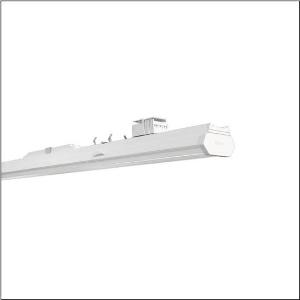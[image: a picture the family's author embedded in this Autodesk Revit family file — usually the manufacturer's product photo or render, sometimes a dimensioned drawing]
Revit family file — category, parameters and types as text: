
# Revit family: licross_r__21_protected_mo_52tp12dn4a5gd_0331
name_source: partatom
category: Lighting Fixtures
units: mm (PartAtom-declared; Revit-internal decimal feet)

## family parameters
Cut with Voids When Loaded = No
Host = Face
Light Source = No
Part Type = Normal
Room Calculation Point = No
Round Connector Dimension = Use Diameter
Shared = No

## types (1)
- --- (1 x LED, 1610 lm, 10.2 W, 4000K)
    Apparent Load = 10 VA
    CIE Flux Codes = 73 92 98 99 100
    Color Rendering = 80
    Color Temperature = 4000K
    Default Elevation = 1800 mm
    Description = Licross® 21 Protected MO, luminaire insert, of sheet steel, galvanised, coil coated, white, length: 1.500mm, width: 90mm, height: 103mm, LED rated luminous flux: 10.700lm, light colour: 840, SDCM (Standard Deviation of Colour Matching)MacAdam ≤ 3 SDCM (initial), control gear: DALI 2 (for two DALI lines), with plug, 6-pole, with phase selection, mains connection: 220..240V, AC/DC, 0/50..60Hz, rated input power: 62W, without changeover relay, for emergency light function, for central battery installations according to EN 60598-2-22, internal wiring halogen-free, primary light control with lens, of plastic, primary optical cover: cover, of PMMA, light emission: direct distribution, primary light characteristic: symmetric, protection rating (complete): IP64, insulation class (complete): insulation class I (protective earthing), certification: CE, ENEC, VDE, UKCA, protection symbol: D if used in an environment with conductive dust loads with corresponding accessories, impact resistance: IK06, permissible ambient temperature for indoor applications: -25..+35°C, standard: EN 60598-2-22, corresponds to IFS (International Featured Standards) requirements for safety and quality in the food industry, reducing of maximum allowable ambient temperature of 5°C with ceiling mounting, LABS conformity tested according to VDMA 24364:2018-05, packaging unit: 1 piece
    Height = 92 mm
    Lamp = 1 x LED
    Lamp Light Flux = 1610 lm
    Lamp Power = 10.2 W
    Lamp count = 1
    Length = 1500 mm
    Luminous efficacy = 158 lm/W
    Manufacturer = Siteco
    ModVariant = No
    Model = 52TP12DN4A5GD
    Mounting Place = Ceiling
    Mounting Type = Pendant
    Number of Poles = 1
    OnlyDefault = Yes
    Power Factor = 1
    Product Name = Licross® 21 Protected MO
    Product group = luminaire insert | ceiling pendant
    ProductGroupID = 901
    Protection Class = Protection class I
    Protection Degree = IP 64
    RLX_Detail_Level = 1
    RLX_Emergency_Light_Flux = 0 lm
    RLX_Emergency_Type = 0
    RLX_Emergency_Type_DB = No
    RlxData = <blob elided: 25073 chars, md5=40d94d71>
    Socket = socket
    Standby Power = 0 W
    System Light Flux = 1610 lm
    System Power = 10 W
    Type Comments = : DC mode (central or group accumulator) initial emergency light level
    Type Image = l_1256148.jpg
    URL = http://relux.com
    VarID = @adj_120207
    Voltage = 0 V
    Weight = 0.00 kg
    Width = 88 mm

## geometry (parser evidence)
native form markers: Blend x4, Sweep x10
no freeform markers — native parametric forms only
